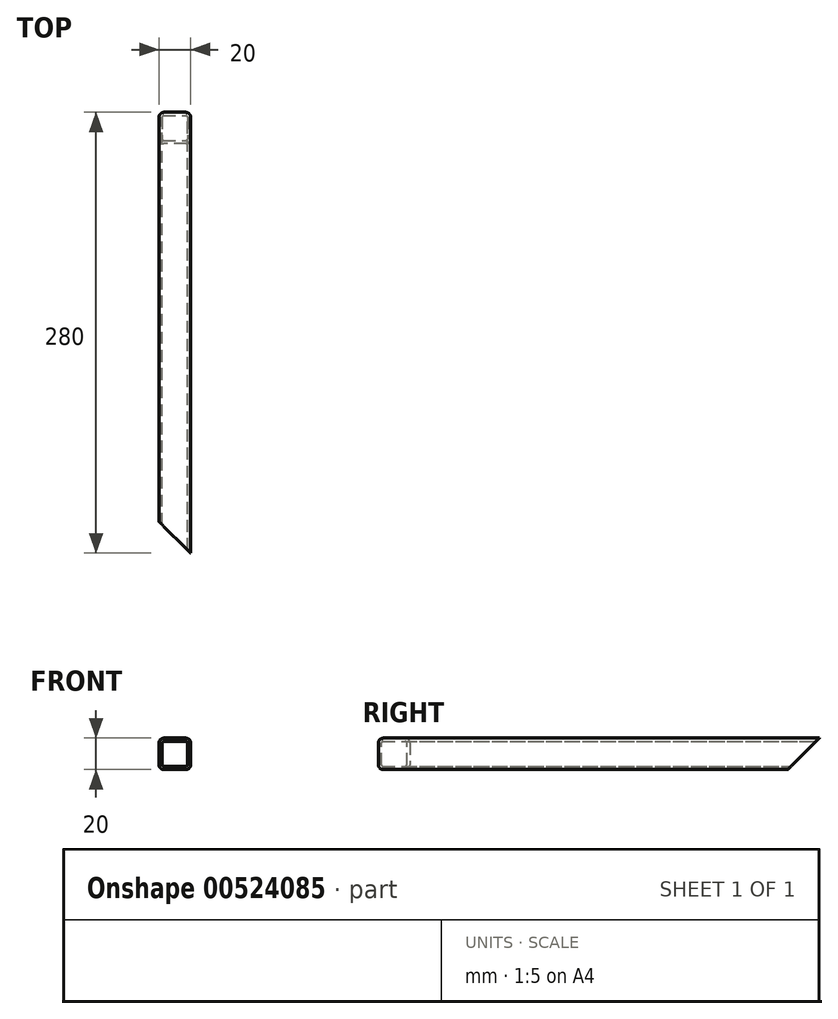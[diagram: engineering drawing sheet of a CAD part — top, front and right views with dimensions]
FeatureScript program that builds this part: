
annotation { "Feature Type Name" : "Feature", "Feature Type Description" : "" }
export const myFeature = defineFeature(function(context is Context, id is Id, definition is map)
    precondition{}
    {
        {
            assignVariable(context, id + "F0", {"name" : "R", "anyValue" : 3});
        }
        {
            assignVariable(context, id + "F1", {"name" : "W", "anyValue" : 2});
        }
        {
            var Q0;
            Q0=qCreatedBy(makeId("Front.planeOp"),FACE);
            var sketch = newSketch(context, id + "F2", { "sketchPlane" : qUnion([Q0])});
            skLineSegment(sketch, "E0.bottom", {"start": v(-10, 10) * mm, "end": v(10, 10) * mm});
            skLineSegment(sketch, "E0.top", {"start": v(-10, -10) * mm, "end": v(10, -10) * mm});
            skLineSegment(sketch, "E0.left", {"start": v(-10, 10) * mm, "end": v(-10, -10) * mm});
            skLineSegment(sketch, "E0.right", {"start": v(10, 10) * mm, "end": v(10, -10) * mm});
            skSolve(sketch);
        }
        {
            var Q0;
            Q0=qSketchRegion(id+"F2",true);
            extrude(context, id + "F3", {"entities" : qUnion([Q0]), "endBound" : BoundingType.SYMMETRIC, "depth" : 280 * mm, "offsetDistance" : 25 * mm});
        }
        {
            var Q0;
            Q0=makeQuery(id+"F3.opExtrude","SWEPT_EDGE",EDGE,{"disambiguationData":[OSD([sQuery(id+"F2.wireOp",EDGE,"E0.bottom"),sQuery(id+"F2.wireOp",EDGE,"E0.right")])]});
            var Q1;
            Q1=makeQuery(id+"F3.opExtrude","SWEPT_EDGE",EDGE,{"disambiguationData":[OSD([sQuery(id+"F2.wireOp",EDGE,"E0.bottom"),sQuery(id+"F2.wireOp",EDGE,"E0.left")])]});
            var Q2;
            Q2=makeQuery(id+"F3.opExtrude","SWEPT_EDGE",EDGE,{"disambiguationData":[OSD([sQuery(id+"F2.wireOp",EDGE,"E0.top"),sQuery(id+"F2.wireOp",EDGE,"E0.right")])]});
            var Q3;
            Q3=makeQuery(id+"F3.opExtrude","SWEPT_EDGE",EDGE,{"disambiguationData":[OSD([sQuery(id+"F2.wireOp",EDGE,"E0.top"),sQuery(id+"F2.wireOp",EDGE,"E0.left")])]});
            fillet(context, id + "F4", {"entities" : qUnion([Q0, Q1, Q2, Q3]), "radius" : (getVariable(context, 'R')) * mm, "tangentPropagation" : true, "allowEdgeOverflow" : false});
        }
        {
            var Q0;
            Q0=makeQuery(id+"F3.opExtrude","CAP_FACE",FACE,{"disambiguationData":[OSD([sQuery(id+"F2.wireOp",EDGE,"E0.bottom"),sQuery(id+"F2.wireOp",EDGE,"E0.top"),sQuery(id+"F2.wireOp",EDGE,"E0.left"),sQuery(id+"F2.wireOp",EDGE,"E0.right")])],"isStart":false});
            var Q1;
            Q1=makeQuery(id+"F3.opExtrude","CAP_FACE",FACE,{"disambiguationData":[OSD([sQuery(id+"F2.wireOp",EDGE,"E0.bottom"),sQuery(id+"F2.wireOp",EDGE,"E0.top"),sQuery(id+"F2.wireOp",EDGE,"E0.left"),sQuery(id+"F2.wireOp",EDGE,"E0.right")])],"isStart":true});
            shell(context, id + "F5", {"entities" : qUnion([Q0, Q1]), "thickness" : (getVariable(context, 'W')) * mm});
        }
        {
            var Q0;
            Q0=makeQuery(id+"F3.opExtrude","SWEPT_FACE",FACE,{"disambiguationData":[OSD([sQuery(id+"F2.wireOp",EDGE,"E0.left")])]});
            var sketch = newSketch(context, id + "F6", { "sketchPlane" : qUnion([Q0])});
            skLineSegment(sketch, "E1", {"start": v(-140, -10) * mm, "end": v(-120, -10) * mm});
            skLineSegment(sketch, "E2", {"start": v(-120, -10) * mm, "end": v(-140, 10) * mm});
            skLineSegment(sketch, "E3", {"start": v(-140, 10) * mm, "end": v(-140, -10) * mm});
            skSolve(sketch);
        }
        {
            var Q0;
            Q0=qSketchRegion(id+"F6",true);
            extrude(context, id + "F7", {"entities" : qUnion([Q0]), "operationType" : NewBodyOperationType.REMOVE, "endBound" : BoundingType.THROUGH_ALL, "oppositeDirection" : true, "depth" : 25 * mm, "offsetDistance" : 25 * mm});
        }
        {
            var Q0;
            Q0=makeQuery(id+"F3.opExtrude","SWEPT_FACE",FACE,{"disambiguationData":[OSD([sQuery(id+"F2.wireOp",EDGE,"E0.top")])]});
            var sketch = newSketch(context, id + "F8", { "sketchPlane" : qUnion([Q0])});
            skLineSegment(sketch, "E4.0", {"start": v(-10, 120) * mm, "end": v(-10, 140) * mm});
            skLineSegment(sketch, "E5", {"start": v(-10, 120) * mm, "end": v(10, 140) * mm});
            skLineSegment(sketch, "E6", {"start": v(10, 140) * mm, "end": v(-10, 140) * mm});
            skPoint(sketch, "E7.orphan", {"position": v(-10, -123) * mm});
            skPoint(sketch, "E8.0.end.orphan", {"position": v(10, -123) * mm});
            skSolve(sketch);
        }
        {
            var Q0;
            Q0=qSketchRegion(id+"F8",true);
            extrude(context, id + "F9", {"entities" : qUnion([Q0]), "operationType" : NewBodyOperationType.REMOVE, "endBound" : BoundingType.THROUGH_ALL, "oppositeDirection" : true, "depth" : 25 * mm, "offsetDistance" : 25 * mm});
        }
    });
